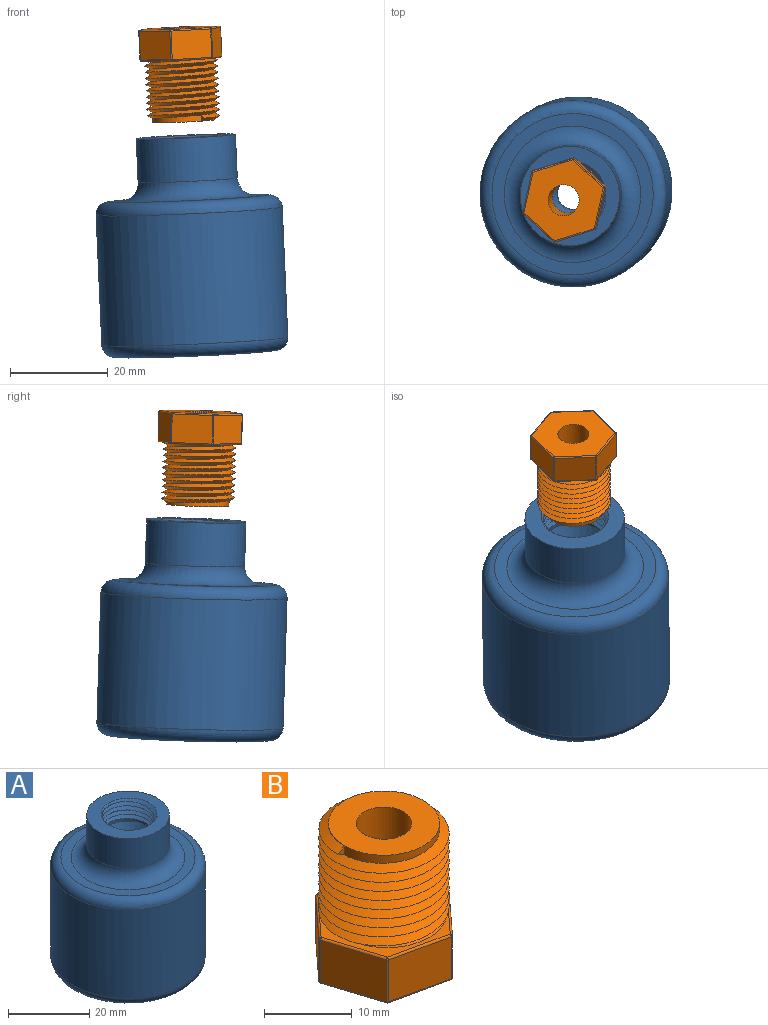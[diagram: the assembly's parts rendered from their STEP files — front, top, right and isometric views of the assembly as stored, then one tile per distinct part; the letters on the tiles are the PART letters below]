
ASSEMBLY  parts=2 mates=1
PART A: 19 faces, bbox 42.1x42.1x46.6 mm
  f0: plane 21.19x21.19mm, normal (0,0,1), area 176mm2, adj f1,f5,f13,f14
  f1: cylinder r=6.35mm len=12.7mm, axis (0,0,-1), area 28.8mm2, adj f0,f6,f13,f14,f15
  f2: cylinder r=19.05mm len=38.1mm, axis (0,0,-1), area 3192.3mm2, adj f11,f12
  f3: plane 33.02x33.02mm, normal (0,0,1), area 243.2mm2, adj f4,f11
  f4: torus R=13.97mm, axis (0,0,-1), area 434.1mm2, adj f3,f5
  f5: cylinder r=10.16mm len=20.32mm, axis (0,0,-1), area 567.5mm2, adj f0,f4
  f6: cone r=6.35mm half-angle=26.6deg, axis (0,0,1), area 212.4mm2, adj f1,f7
  f7: cylinder r=3.17mm len=6.35mm, axis (0,0,-1), area 63.3mm2, adj f6,f8
  f8: plane 31.75x31.75mm, normal (0,0,-1), area 760.1mm2, adj f7,f9
  f9: cylinder r=15.88mm len=31.75mm, axis (0,0,-1), area 228.3mm2, adj f8,f10,f16,f17,f18
  f10: plane 33.68x33.68mm, normal (0,0,-1), area 32.6mm2, adj f9,f12,f17,f18
  f11: torus R=16.51mm, axis (0,0,1), area 454.4mm2, adj f2,f3
  f12: torus R=16.51mm, axis (0,0,-1), area 454.4mm2, adj f2,f10,f17,f18
  f13: bspline ~17.09x14.8mm, area 250.4mm2, adj f0,f1,f14,f15
  f14: bspline ~17.09x14.8mm, area 225.1mm2, adj f0,f1,f13,f15
  f15: plane 1.24x1.05mm, normal (0,-1,0), area 0.7mm2, adj f1,f13,f14
  f16: plane 0.76x0.66mm, normal (0,1,0), area 0.3mm2, adj f9,f17,f18
  f17: bspline ~38.19x33.07mm, area 2741.6mm2, adj f9,f10,f12,f16,f18
  f18: bspline ~38.19x33.07mm, area 2781.6mm2, adj f9,f10,f12,f16,f17
PART B: 44 faces, bbox 18x18x19.9 mm
  f0: plane 17.5x17.11mm, normal (0,0,1), area 39mm2, adj f1,f22,f23,f30,f31,f35,f36,f42
  f1: cylinder r=6.35mm len=12.7mm, axis (0,0,-1), area 47.2mm2, adj f0,f9,f41,f42,f43
  f2: plane 8.11x5.84mm, normal (0.95,0.3,0), area 49.7mm2, adj f11,f32,f36,f38
  f3: plane 8.3x5.84mm, normal (0.22,0.98,0), area 49.7mm2, adj f10,f24,f31,f32
  f4: plane 6.27x5.84mm, normal (-0.74,0.68,0), area 49.7mm2, adj f12,f17,f23,f24
  f5: plane 8.11x5.84mm, normal (-0.95,-0.3,0), area 49.7mm2, adj f14,f17,f21,f22
  f6: plane 8.3x5.84mm, normal (-0.22,-0.98,0), area 49.7mm2, adj f15,f21,f29,f30
  f7: plane 6.27x5.84mm, normal (0.74,-0.68,0), area 49.7mm2, adj f13,f29,f35,f38
  f8: plane 16.61x16.22mm, normal (0,0,-1), area 156.3mm2, adj f10,f11,f12,f13,f14,f15,f40
  f9: plane 12.7x12.7mm, normal (0,0,1), area 95mm2, adj f1,f40
  f10: cylinder r=0.25mm len=8.36mm, axis (0.98,-0.22,0), area 3.4mm2, adj f3,f8,f20,f28
  f11: cylinder r=0.25mm len=8.19mm, axis (0.3,-0.95,0), area 3.4mm2, adj f2,f8,f28,f39
  f12: cylinder r=0.25mm len=6.44mm, axis (0.68,0.74,0), area 3.4mm2, adj f4,f8,f16,f20
  f13: cylinder r=0.25mm len=6.44mm, axis (-0.68,-0.74,0), area 3.4mm2, adj f7,f8,f25,f39
  f14: cylinder r=0.25mm len=8.19mm, axis (-0.3,0.95,0), area 3.4mm2, adj f5,f8,f16,f18
  f15: cylinder r=0.25mm len=8.36mm, axis (-0.98,0.22,0), area 3.4mm2, adj f6,f8,f18,f25
  f16: sphere r=0.25mm, area 0.1mm2, adj f12,f14,f17
  f17: cylinder r=0.25mm len=5.84mm, axis (0,0,1), area 1.6mm2, adj f4,f5,f16,f19
  f18: sphere r=0.25mm, area 0.1mm2, adj f14,f15,f21
  f19: sphere r=0.25mm, area 0.1mm2, adj f17,f22,f23
  f20: sphere r=0.25mm, area 0.1mm2, adj f10,f12,f24
  f21: cylinder r=0.25mm len=5.84mm, axis (0,0,1), area 1.6mm2, adj f5,f6,f18,f26
  f22: cylinder r=0.25mm len=8.19mm, axis (0.3,-0.95,0), area 3.4mm2, adj f0,f5,f19,f26
  f23: cylinder r=0.25mm len=6.44mm, axis (-0.68,-0.74,0), area 3.4mm2, adj f0,f4,f19,f27
  f24: cylinder r=0.25mm len=5.84mm, axis (0,0,1), area 1.6mm2, adj f3,f4,f20,f27
  f25: sphere r=0.25mm, area 0.1mm2, adj f13,f15,f29
  f26: sphere r=0.25mm, area 0.1mm2, adj f21,f22,f30
  f27: sphere r=0.25mm, area 0.1mm2, adj f23,f24,f31
  f28: sphere r=0.25mm, area 0mm2, adj f10,f11,f32
  f29: cylinder r=0.25mm len=5.84mm, axis (0,0,1), area 1.6mm2, adj f6,f7,f25,f33
  f30: cylinder r=0.25mm len=8.36mm, axis (0.98,-0.22,0), area 3.4mm2, adj f0,f6,f26,f33
  f31: cylinder r=0.25mm len=8.36mm, axis (-0.98,0.22,0), area 3.4mm2, adj f0,f3,f27,f34
  f32: cylinder r=0.25mm len=5.84mm, axis (0,0,1), area 1.6mm2, adj f2,f3,f28,f34
  f33: sphere r=0.25mm, area 0.1mm2, adj f29,f30,f35
  f34: sphere r=0.25mm, area 0mm2, adj f31,f32,f36
  f35: cylinder r=0.25mm len=6.44mm, axis (0.68,0.74,0), area 3.4mm2, adj f0,f7,f33,f37
  f36: cylinder r=0.25mm len=8.19mm, axis (-0.3,0.95,0), area 3.4mm2, adj f0,f2,f34,f37
  f37: sphere r=0.25mm, area 0.1mm2, adj f35,f36,f38
  f38: cylinder r=0.25mm len=5.84mm, axis (0,0,1), area 1.6mm2, adj f2,f7,f37,f39
  f39: sphere r=0.25mm, area 0mm2, adj f11,f13,f38
  f40: cylinder r=3.17mm len=19.05mm, axis (0,0,-1), area 380mm2, adj f8,f9
  f41: plane 1.24x1.08mm, normal (0,-1,0), area 0.7mm2, adj f1,f42,f43
  f42: bspline ~17.15x14.86mm, area 499.4mm2, adj f0,f1,f41,f43
  f43: bspline ~17.15x14.86mm, area 524.4mm2, adj f0,f1,f41,f42
PLACE A rot(axis=(0.03,-0.09,1),35deg) t=(15.72,-4.75,-61.8)mm
PLACE B rot(axis=(0.46,0.89,0.02),178.6deg) t=(12.76,-6.84,-1.59)mm
MATE cylindrical B.f1 <-> A.f0  axis (-0.04,-0.03,1) through (12.91,-6.74,-4.76)mm
